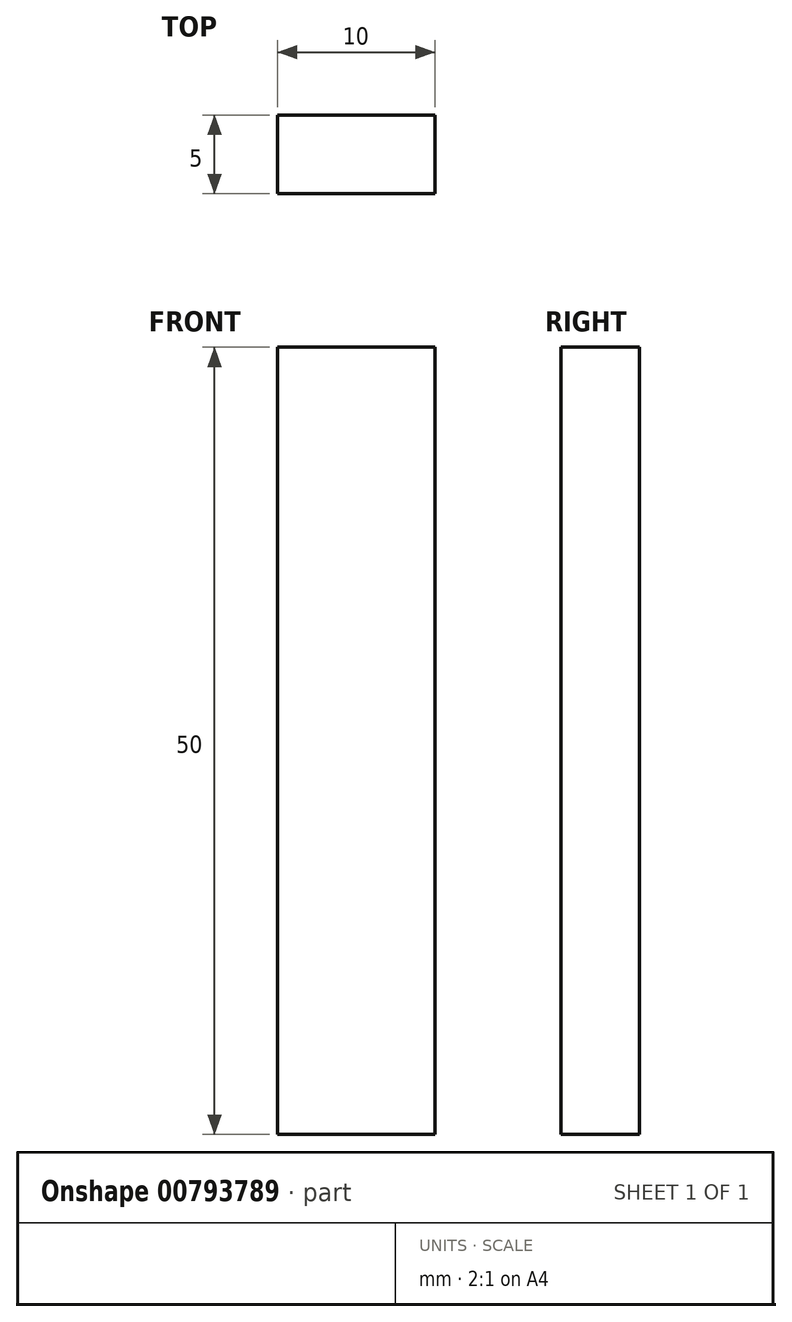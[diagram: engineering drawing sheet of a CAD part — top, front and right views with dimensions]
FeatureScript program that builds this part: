
annotation { "Feature Type Name" : "Feature", "Feature Type Description" : "" }
export const myFeature = defineFeature(function(context is Context, id is Id, definition is map)
    precondition{}
    {
        {
            var Q0;
            Q0=qCreatedBy(makeId("Front.planeOp"),FACE);
            var sketch = newSketch(context, id + "F0", { "sketchPlane" : qUnion([Q0])});
            skLineSegment(sketch, "E0.bottom", {"start": v(5, -25) * mm, "end": v(-5, -25) * mm});
            skLineSegment(sketch, "E0.top", {"start": v(5, 25) * mm, "end": v(-5, 25) * mm});
            skLineSegment(sketch, "E0.left", {"start": v(5, -25) * mm, "end": v(5, 25) * mm});
            skLineSegment(sketch, "E0.right", {"start": v(-5, -25) * mm, "end": v(-5, 25) * mm});
            skPoint(sketch, "E0.middle", {"position": v(0, 0) * mm});
            skSolve(sketch);
        }
        {
            var Q0;
            Q0=makeQuery(id+"F0.imprint","IMPRINT",FACE,{"disambiguationData":[TD([[makeQuery(id+"F0.imprint","IMPRINT",EDGE,{"derivedFrom":sQuery(id+"F0.wireOp",EDGE,"E0.bottom")}),-1.0]])]});
            extrude(context, id + "F1", {"entities" : qUnion([Q0]), "depth" : 5 * mm, "offsetDistance" : 25 * mm});
        }
    });
